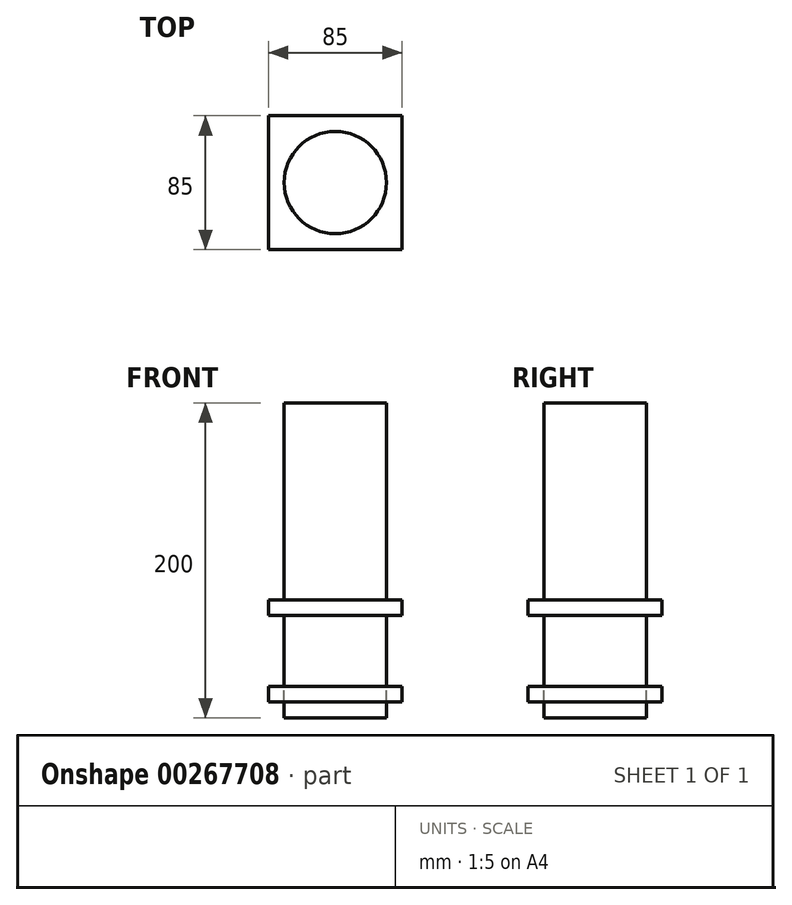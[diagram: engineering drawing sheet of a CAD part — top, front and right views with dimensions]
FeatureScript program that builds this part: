
annotation { "Feature Type Name" : "Feature", "Feature Type Description" : "" }
export const myFeature = defineFeature(function(context is Context, id is Id, definition is map)
    precondition{}
    {
        {
            var Q0;
            Q0=qCreatedBy(makeId("Front.planeOp"),FACE);
            var sketch = newSketch(context, id + "F0", { "sketchPlane" : qUnion([Q0])});
            skLineSegment(sketch, "E0", {"start": v(0, -10) * mm, "end": v(-32.5, -10) * mm});
            skLineSegment(sketch, "E1", {"start": v(-32.5, -10) * mm, "end": v(-32.5, 190) * mm});
            skLineSegment(sketch, "E2", {"start": v(-32.5, 190) * mm, "end": v(0, 190) * mm});
            skLineSegment(sketch, "E3", {"start": v(0, 190) * mm, "end": v(0, -10) * mm});
            skSolve(sketch);
        }
        {
            var Q0;
            Q0 = qSketchRegion(id + "F0", true);
            var Q1;
            Q1=sQuery(id+"F0.wireOp",EDGE,"E3");
            revolve(context, id + "F1", {"entities" : qUnion([Q0]), "axis" : qUnion([Q1]), "revolveType" : RevolveType.FULL});
        }
        {
            var Q0;
            Q0=qCreatedBy(makeId("Top.planeOp"),FACE);
            var sketch = newSketch(context, id + "F2", { "sketchPlane" : qUnion([Q0])});
            skLineSegment(sketch, "E4.bottom", {"start": v(42.5, 42.5) * mm, "end": v(-42.5, 42.5) * mm});
            skLineSegment(sketch, "E4.top", {"start": v(42.5, -42.5) * mm, "end": v(-42.5, -42.5) * mm});
            skLineSegment(sketch, "E4.left", {"start": v(42.5, 42.5) * mm, "end": v(42.5, -42.5) * mm});
            skLineSegment(sketch, "E4.right", {"start": v(-42.5, 42.5) * mm, "end": v(-42.5, -42.5) * mm});
            skPoint(sketch, "E4.middle", {"position": v(0, 0) * mm});
            skSolve(sketch);
        }
        {
            var Q0;
            Q0=makeQuery(id+"F2.imprint","IMPRINT",FACE,{"disambiguationData":[TD([[makeQuery(id+"F2.imprint","IMPRINT",EDGE,{"derivedFrom":sQuery(id+"F2.wireOp",EDGE,"E4.bottom")}),1.0]])]});
            var Q1;
            Q1=sQuery(id+"F2.wireOp",EDGE,"E4.right");
            extrude(context, id + "F3", {"entities" : qUnion([Q0]), "surfaceEntities" : qUnion([Q1]), "depth" : 10 * mm});
        }
        {
            var Q0;
            Q0=qCreatedBy(makeId("Top.planeOp"),FACE);
            cPlane(context, id + "F4", {"entities" : qUnion([Q0]), "cplaneType" : CPlaneType.OFFSET, "offset" : 65 * mm, "width" : 150 * mm, "height" : 150 * mm});
        }
        {
            var Q0;
            Q0=qCreatedBy(id+"F4.planeOp",FACE);
            var sketch = newSketch(context, id + "F5", { "sketchPlane" : qUnion([Q0])});
            skLineSegment(sketch, "E5.bottom", {"start": v(42.5, 42.5) * mm, "end": v(-42.5, 42.5) * mm});
            skLineSegment(sketch, "E5.top", {"start": v(42.5, -42.5) * mm, "end": v(-42.5, -42.5) * mm});
            skLineSegment(sketch, "E5.left", {"start": v(42.5, 42.5) * mm, "end": v(42.5, -42.5) * mm});
            skLineSegment(sketch, "E5.right", {"start": v(-42.5, 42.5) * mm, "end": v(-42.5, -42.5) * mm});
            skPoint(sketch, "E5.middle", {"position": v(0, 0) * mm});
            skSolve(sketch);
        }
        {
            var Q0;
            Q0=makeQuery(id+"F5.imprint","IMPRINT",FACE,{"disambiguationData":[TD([[makeQuery(id+"F5.imprint","IMPRINT",EDGE,{"derivedFrom":sQuery(id+"F5.wireOp",EDGE,"E5.bottom")}),1.0]])]});
            extrude(context, id + "F6", {"entities" : qUnion([Q0]), "operationType" : NewBodyOperationType.ADD, "oppositeDirection" : true, "depth" : 10 * mm});
        }
    });
